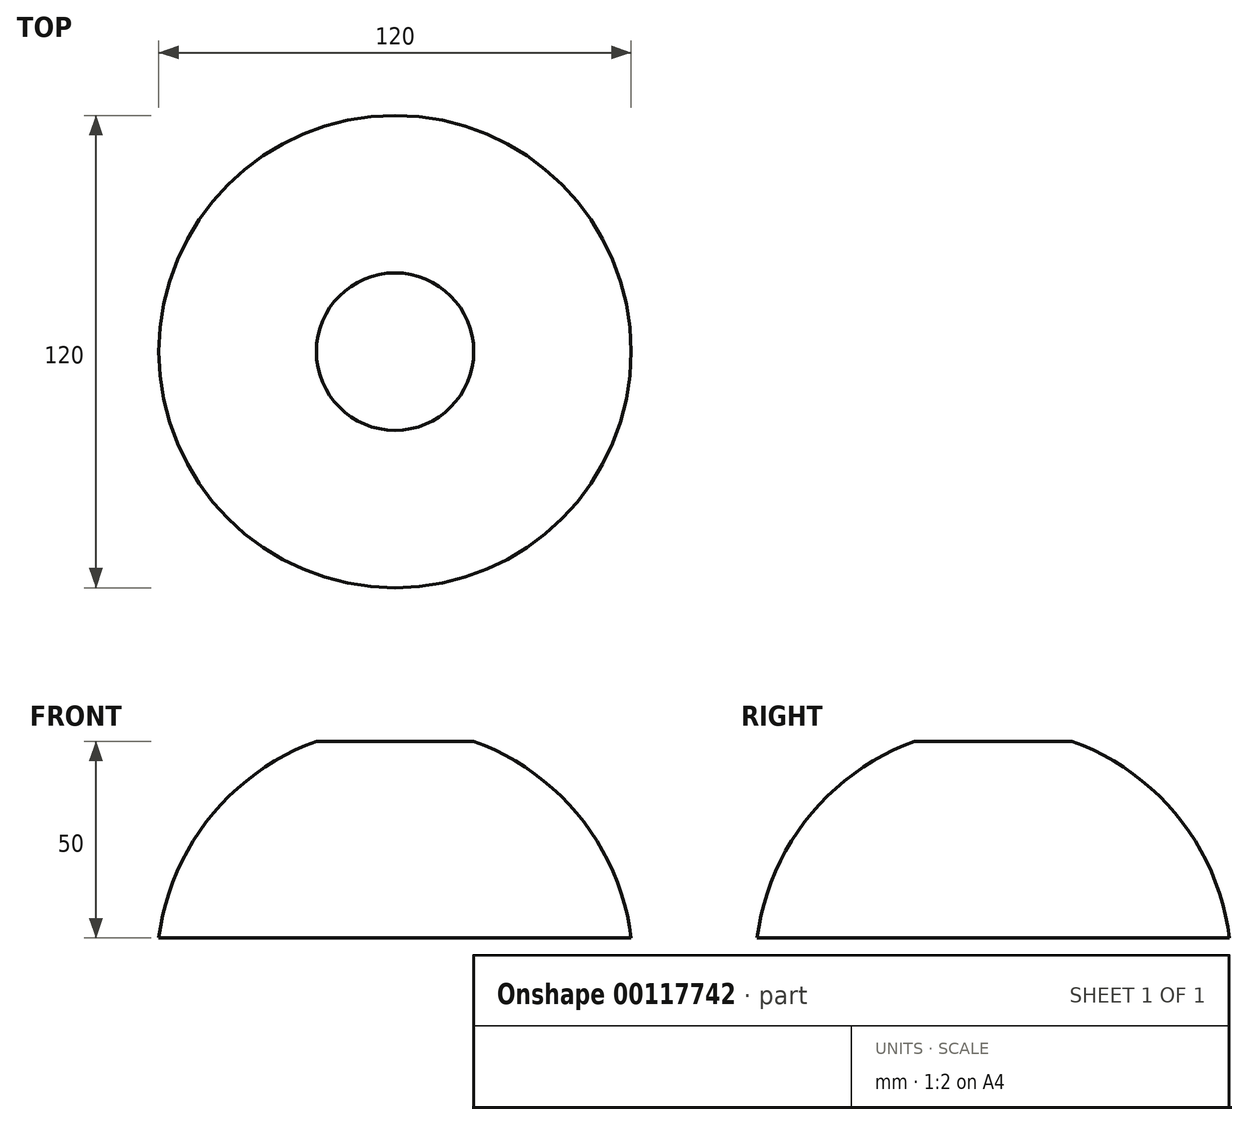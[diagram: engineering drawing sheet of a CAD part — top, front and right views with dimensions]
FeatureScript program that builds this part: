
annotation { "Feature Type Name" : "Feature", "Feature Type Description" : "" }
export const myFeature = defineFeature(function(context is Context, id is Id, definition is map)
    precondition{}
    {
        {
            var Q0;
            Q0=qCreatedBy(makeId("Front.planeOp"),FACE);
            var sketch = newSketch(context, id + "F0", { "sketchPlane" : qUnion([Q0])});
            skLineSegment(sketch, "E0", {"start": v(0, 0) * mm, "end": v(0, 50) * mm});
            skLineSegment(sketch, "E1", {"start": v(0, 0) * mm, "end": v(60, 0) * mm});
            skLineSegment(sketch, "E2", {"start": v(0, 50) * mm, "end": v(20, 50) * mm});
            skArc(sketch, "E3", {"start": v(60, 0) * mm, "mid": v(47.06, 30.64) * mm, "end": v(20, 50) * mm});
            skSolve(sketch);
        }
        {
            var Q0;
            Q0=makeQuery(id+"F0.imprint","IMPRINT",FACE,{"disambiguationData":[TD([[makeQuery(id+"F0.imprint","IMPRINT",EDGE,{"derivedFrom":sQuery(id+"F0.wireOp",EDGE,"E0")}),-1.0]])]});
            var Q1;
            Q1=sQuery(id+"F0.wireOp",EDGE,"E0");
            revolve(context, id + "F1", {"entities" : qUnion([Q0]), "axis" : qUnion([Q1]), "revolveType" : RevolveType.FULL});
        }
    });
